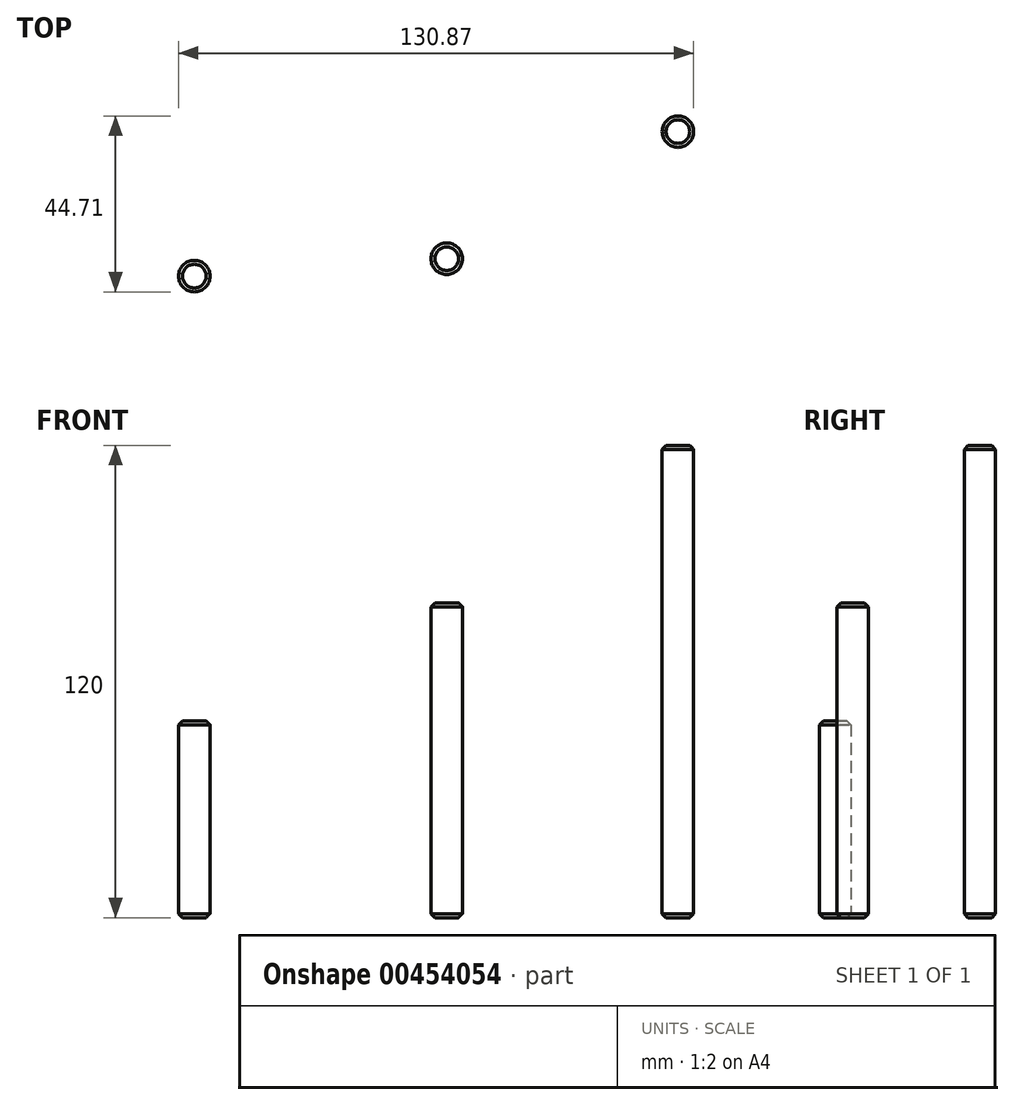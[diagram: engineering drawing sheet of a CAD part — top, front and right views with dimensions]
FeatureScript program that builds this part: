
annotation { "Feature Type Name" : "Feature", "Feature Type Description" : "" }
export const myFeature = defineFeature(function(context is Context, id is Id, definition is map)
    precondition{}
    {
        {
            var Q0;
            Q0=qCreatedBy(makeId("Top.planeOp"),FACE);
            var sketch = newSketch(context, id + "F0", { "sketchPlane" : qUnion([Q0])});
            skCircle(sketch, "E0", {"center": v(0, 0) * mm, "radius": 4 * mm});
            skSolve(sketch);
        }
        {
            var Q0;
            Q0 = qSketchRegion(id + "F0", true);
            extrude(context, id + "F1", {"entities" : qUnion([Q0]), "depth" : 120 * mm, "offsetDistance" : 25 * mm});
        }
        {
            var Q0;
            Q0=makeQuery(id+"F1.opExtrude","CAP_EDGE",EDGE,{"disambiguationData":[OSD([sQuery(id+"F0.wireOp",EDGE,"E0")])],"isStart":false});
            var Q1;
            Q1=makeQuery(id+"F1.opExtrude","CAP_EDGE",EDGE,{"disambiguationData":[OSD([sQuery(id+"F0.wireOp",EDGE,"E0")])],"isStart":true});
            chamfer(context, id + "F2", {"entities" : qUnion([Q0, Q1]), "width" : 1 * mm, "tangentPropagation" : true});
        }
        {
            var Q0;
            Q0=qCreatedBy(makeId("Top.planeOp"),FACE);
            var sketch = newSketch(context, id + "F3", { "sketchPlane" : qUnion([Q0])});
            skCircle(sketch, "E1", {"center": v(-122.87, -36.71) * mm, "radius": 4 * mm});
            skSolve(sketch);
        }
        {
            var Q0;
            Q0 = qSketchRegion(id + "F3", true);
            extrude(context, id + "F4", {"entities" : qUnion([Q0]), "depth" : 50 * mm, "offsetDistance" : 25 * mm});
        }
        {
            var Q0;
            Q0=makeQuery(id+"F4.opExtrude","CAP_EDGE",EDGE,{"disambiguationData":[OSD([sQuery(id+"F3.wireOp",EDGE,"E1")])],"isStart":false});
            var Q1;
            Q1=makeQuery(id+"F4.opExtrude","CAP_EDGE",EDGE,{"disambiguationData":[OSD([sQuery(id+"F3.wireOp",EDGE,"E1")])],"isStart":true});
            chamfer(context, id + "F5", {"entities" : qUnion([Q0, Q1]), "width" : 1 * mm, "tangentPropagation" : true});
        }
        {
            var Q0;
            Q0=qCreatedBy(makeId("Top.planeOp"),FACE);
            var sketch = newSketch(context, id + "F6", { "sketchPlane" : qUnion([Q0])});
            skCircle(sketch, "E2", {"center": v(-58.75, -32.3) * mm, "radius": 4 * mm});
            skSolve(sketch);
        }
        {
            var Q0;
            Q0 = qSketchRegion(id + "F6", true);
            extrude(context, id + "F7", {"entities" : qUnion([Q0]), "depth" : 80 * mm, "offsetDistance" : 25 * mm});
        }
        {
            var Q0;
            Q0=makeQuery(id+"F7.opExtrude","CAP_EDGE",EDGE,{"disambiguationData":[OSD([sQuery(id+"F6.wireOp",EDGE,"E2")])],"isStart":false});
            var Q1;
            Q1=makeQuery(id+"F7.opExtrude","CAP_EDGE",EDGE,{"disambiguationData":[OSD([sQuery(id+"F6.wireOp",EDGE,"E2")])],"isStart":true});
            chamfer(context, id + "F8", {"entities" : qUnion([Q0, Q1]), "width" : 1 * mm, "tangentPropagation" : true});
        }
    });
